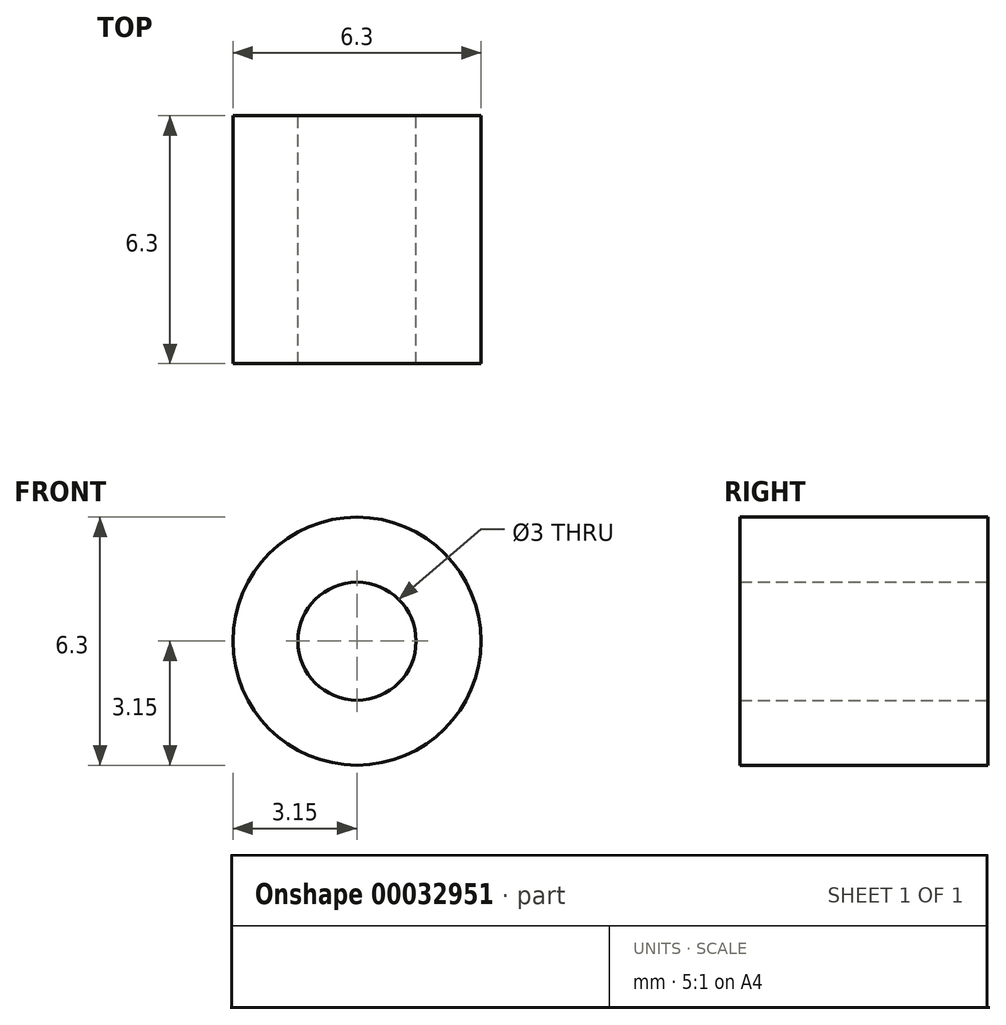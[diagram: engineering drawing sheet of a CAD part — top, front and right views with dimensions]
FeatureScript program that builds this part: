
annotation { "Feature Type Name" : "Feature", "Feature Type Description" : "" }
export const myFeature = defineFeature(function(context is Context, id is Id, definition is map)
    precondition{}
    {
        {
            var Q0;
            Q0=qCreatedBy(makeId("Front.planeOp"),FACE);
            var sketch = newSketch(context, id + "F0", { "sketchPlane" : qUnion([Q0])});
            skCircle(sketch, "E0", {"center": v(0, 0) * mm, "radius": 1.5 * mm});
            skCircle(sketch, "E1", {"center": v(0, 0) * mm, "radius": 3.15 * mm});
            skSolve(sketch);
        }
        {
            var Q0;
            Q0=qSketchRegion(id+"F0",true);
            extrude(context, id + "F1", {"entities" : qUnion([Q0]), "depth" : 6.3 * mm});
        }
    });
